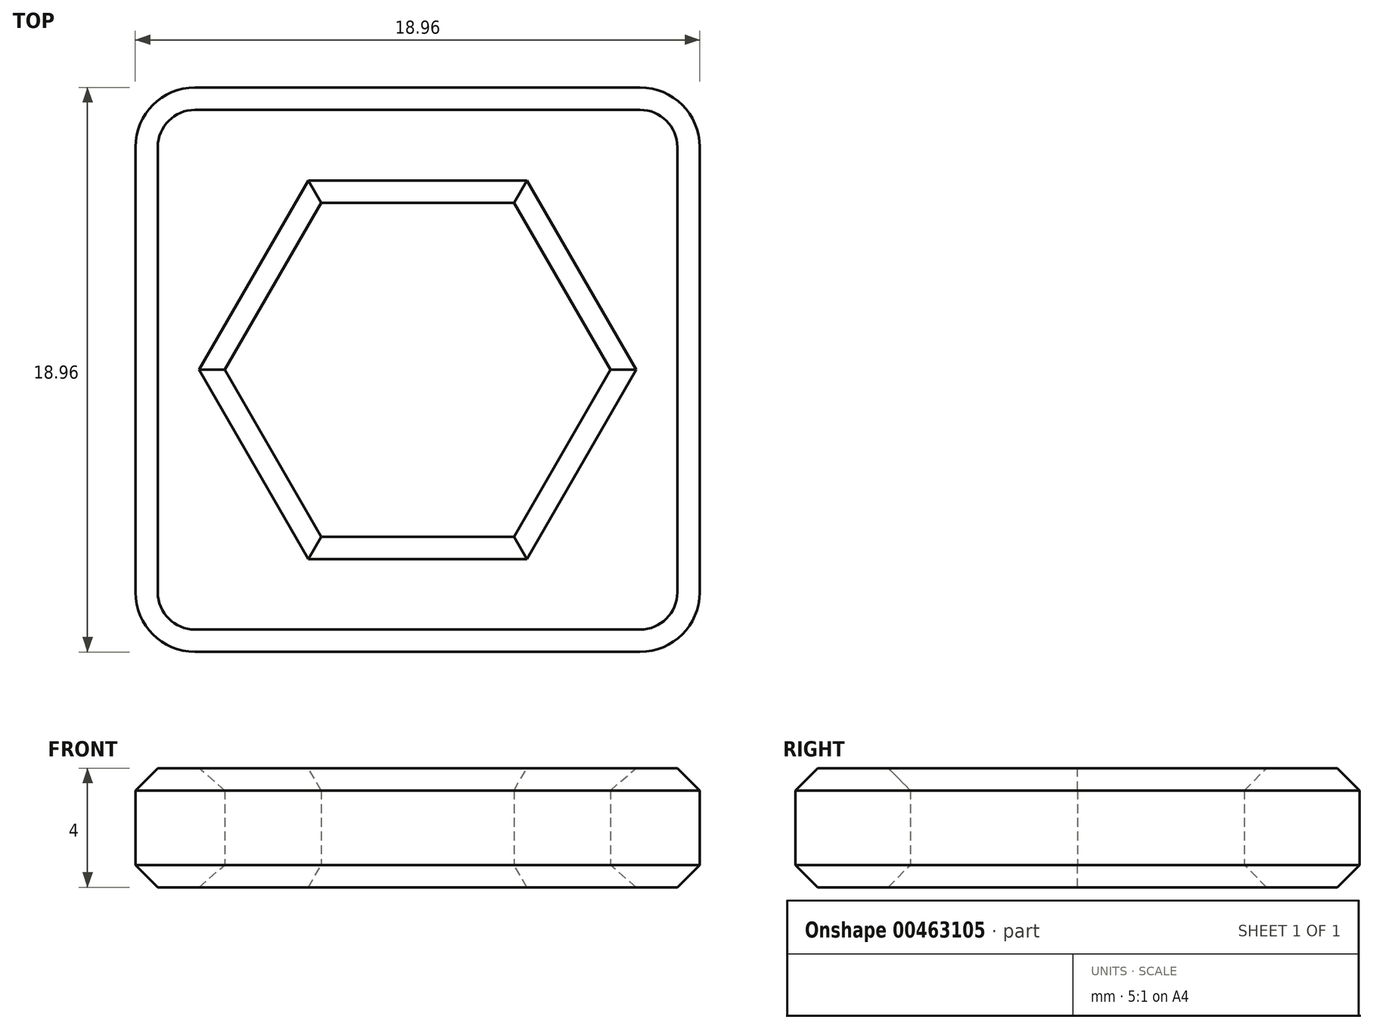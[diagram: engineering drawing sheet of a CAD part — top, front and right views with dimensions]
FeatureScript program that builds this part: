
annotation { "Feature Type Name" : "Feature", "Feature Type Description" : "" }
export const myFeature = defineFeature(function(context is Context, id is Id, definition is map)
    precondition{}
    {
        {
            var Q0;
            Q0=qCreatedBy(makeId("Top.planeOp"),FACE);
            var sketch = newSketch(context, id + "F0", { "sketchPlane" : qUnion([Q0])});
            skLineSegment(sketch, "E0.bottom", {"start": v(9.48, 9.47) * mm, "end": v(-9.47, 9.47) * mm});
            skLineSegment(sketch, "E0.top", {"start": v(9.47, -9.47) * mm, "end": v(-9.47, -9.47) * mm});
            skLineSegment(sketch, "E0.left", {"start": v(9.48, 9.47) * mm, "end": v(9.47, -9.47) * mm});
            skLineSegment(sketch, "E0.right", {"start": v(-9.47, 9.47) * mm, "end": v(-9.47, -9.47) * mm});
            skPoint(sketch, "E0.middle", {"position": v(0, 0) * mm});
            skCircle(sketch, "E1.cCircle", {"center": v(0, 0) * mm, "radius": 5.6 * mm, "construction": true});
            skLineSegment(sketch, "E1.0", {"start": v(-3.24, 5.6) * mm, "end": v(3.24, 5.6) * mm});
            skLineSegment(sketch, "E1.1", {"start": v(3.24, 5.6) * mm, "end": v(6.47, 0) * mm});
            skLineSegment(sketch, "E1.2", {"start": v(6.47, 0) * mm, "end": v(3.24, -5.6) * mm});
            skLineSegment(sketch, "E1.3", {"start": v(3.24, -5.6) * mm, "end": v(-3.24, -5.6) * mm});
            skLineSegment(sketch, "E1.4", {"start": v(-3.24, -5.6) * mm, "end": v(-6.47, 0) * mm});
            skLineSegment(sketch, "E1.5", {"start": v(-6.47, 0) * mm, "end": v(-3.24, 5.6) * mm});
            skPoint(sketch, "E1.0.midPoint", {"position": v(0, 5.6) * mm});
            skSolve(sketch);
        }
        {
            var Q0;
            Q0 = qSketchRegion(id + "F0", true);
            extrude(context, id + "F1", {"entities" : qUnion([Q0]), "depth" : 4 * mm});
        }
        {
            var Q0;
            Q0=makeQuery(id+"F1.opExtrude","SWEPT_EDGE",EDGE,{"disambiguationData":[OSD([sQuery(id+"F0.wireOp",EDGE,"E0.top"),sQuery(id+"F0.wireOp",EDGE,"E0.left")])]});
            var Q1;
            Q1=makeQuery(id+"F1.opExtrude","SWEPT_EDGE",EDGE,{"disambiguationData":[OSD([sQuery(id+"F0.wireOp",EDGE,"E0.bottom"),sQuery(id+"F0.wireOp",EDGE,"E0.left")])]});
            var Q2;
            Q2=makeQuery(id+"F1.opExtrude","SWEPT_EDGE",EDGE,{"disambiguationData":[OSD([sQuery(id+"F0.wireOp",EDGE,"E0.top"),sQuery(id+"F0.wireOp",EDGE,"E0.right")])]});
            var Q3;
            Q3=makeQuery(id+"F1.opExtrude","SWEPT_EDGE",EDGE,{"disambiguationData":[OSD([sQuery(id+"F0.wireOp",EDGE,"E0.bottom"),sQuery(id+"F0.wireOp",EDGE,"E0.right")])]});
            fillet(context, id + "F2", {"entities" : qUnion([Q0, Q1, Q2, Q3]), "radius" : 2 * mm, "tangentPropagation" : true, "allowEdgeOverflow" : false});
        }
        {
            var Q0;
            Q0=makeQuery(id+"F1.opExtrude","CAP_FACE",FACE,{"disambiguationData":[OSD([sQuery(id+"F0.wireOp",EDGE,"E0.bottom"),sQuery(id+"F0.wireOp",EDGE,"E0.top"),sQuery(id+"F0.wireOp",EDGE,"E0.left"),sQuery(id+"F0.wireOp",EDGE,"E0.right"),sQuery(id+"F0.wireOp",EDGE,"E1.0"),sQuery(id+"F0.wireOp",EDGE,"E1.1"),sQuery(id+"F0.wireOp",EDGE,"E1.2"),sQuery(id+"F0.wireOp",EDGE,"E1.3"),sQuery(id+"F0.wireOp",EDGE,"E1.4"),sQuery(id+"F0.wireOp",EDGE,"E1.5")])],"isStart":false});
            var Q1;
            Q1=makeQuery(id+"F1.opExtrude","CAP_FACE",FACE,{"disambiguationData":[OSD([sQuery(id+"F0.wireOp",EDGE,"E0.bottom"),sQuery(id+"F0.wireOp",EDGE,"E0.top"),sQuery(id+"F0.wireOp",EDGE,"E0.left"),sQuery(id+"F0.wireOp",EDGE,"E0.right"),sQuery(id+"F0.wireOp",EDGE,"E1.0"),sQuery(id+"F0.wireOp",EDGE,"E1.1"),sQuery(id+"F0.wireOp",EDGE,"E1.2"),sQuery(id+"F0.wireOp",EDGE,"E1.3"),sQuery(id+"F0.wireOp",EDGE,"E1.4"),sQuery(id+"F0.wireOp",EDGE,"E1.5")])],"isStart":true});
            chamfer(context, id + "F3", {"entities" : qUnion([Q0, Q1]), "width" : .75 * mm, "tangentPropagation" : true});
        }
    });
